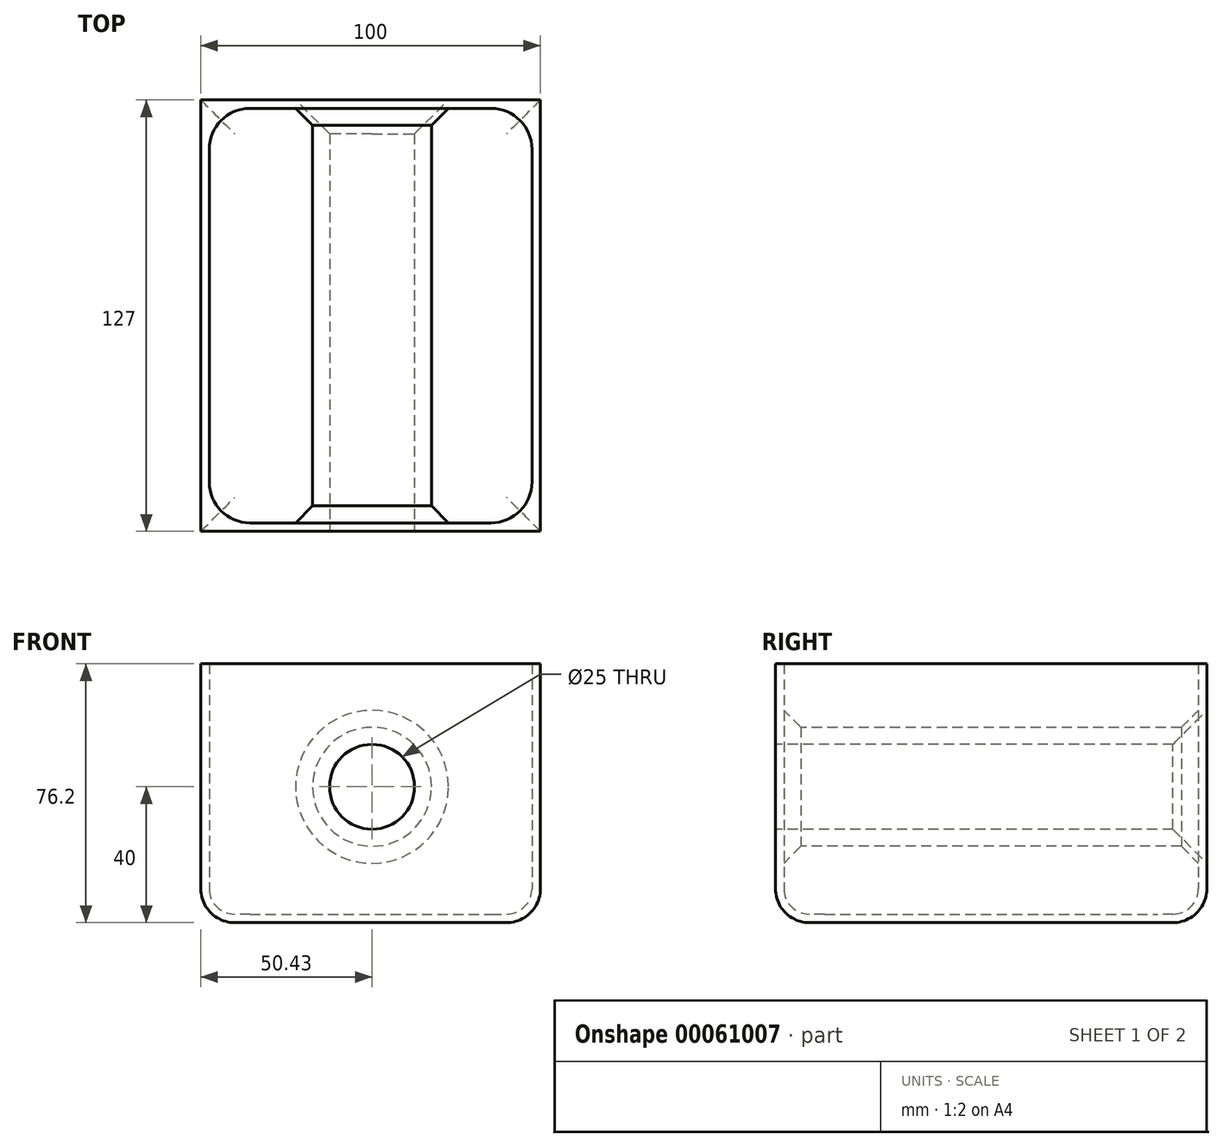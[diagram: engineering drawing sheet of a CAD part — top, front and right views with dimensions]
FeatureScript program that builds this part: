
annotation { "Feature Type Name" : "Feature", "Feature Type Description" : "" }
export const myFeature = defineFeature(function(context is Context, id is Id, definition is map)
    precondition{}
    {
        {
            var Q0;
            Q0=qCreatedBy(makeId("Top.planeOp"),FACE);
            var sketch = newSketch(context, id + "F0", { "sketchPlane" : qUnion([Q0])});
            skLineSegment(sketch, "E0.bottom", {"start": v(-50.43, -48.94) * mm, "end": v(49.57, -48.94) * mm});
            skLineSegment(sketch, "E0.top", {"start": v(-50.43, 78.06) * mm, "end": v(49.57, 78.06) * mm});
            skLineSegment(sketch, "E0.left", {"start": v(-50.43, -48.94) * mm, "end": v(-50.43, 78.06) * mm});
            skLineSegment(sketch, "E0.right", {"start": v(49.57, -48.94) * mm, "end": v(49.57, 78.06) * mm});
            skSolve(sketch);
        }
        {
            var Q0;
            Q0 = qSketchRegion(id + "F0", true);
            extrude(context, id + "F1", {"entities" : qUnion([Q0]), "depth" : 76.2 * mm});
        }
        {
            var Q0;
            Q0=makeQuery(id+"F1.opExtrude","CAP_FACE",FACE,{"disambiguationData":[OSD([sQuery(id+"F0.wireOp",EDGE,"E0.bottom"),sQuery(id+"F0.wireOp",EDGE,"E0.top"),sQuery(id+"F0.wireOp",EDGE,"E0.left"),sQuery(id+"F0.wireOp",EDGE,"E0.right")])],"isStart":true});
            fillet(context, id + "F2", {"entities" : qUnion([Q0]), "radius" : 10 * mm, "tangentPropagation" : true, "allowEdgeOverflow" : false});
        }
        {
            var Q0;
            Q0=makeQuery(id+"F1.opExtrude","CAP_FACE",FACE,{"disambiguationData":[OSD([sQuery(id+"F0.wireOp",EDGE,"E0.bottom"),sQuery(id+"F0.wireOp",EDGE,"E0.top"),sQuery(id+"F0.wireOp",EDGE,"E0.left"),sQuery(id+"F0.wireOp",EDGE,"E0.right")])],"isStart":false});
            shell(context, id + "F3", {"entities" : qUnion([Q0]), "thickness" : 2.5 * mm});
        }
        {
            var Q0;
            Q0=makeQuery(id+"F1.opExtrude","SWEPT_FACE",FACE,{"disambiguationData":[OSD([sQuery(id+"F0.wireOp",EDGE,"E0.bottom")])]});
            var sketch = newSketch(context, id + "F4", { "sketchPlane" : qUnion([Q0])});
            skCircle(sketch, "E1", {"center": v(0, 40) * mm, "radius": 17.5 * mm});
            skSolve(sketch);
        }
        {
            var Q0;
            Q0=makeQuery(id+"F4.imprint","IMPRINT",FACE,{"disambiguationData":[TD([[makeQuery(id+"F4.imprint","IMPRINT",EDGE,{"derivedFrom":sQuery(id+"F4.wireOp",EDGE,"E1")}),1.0]])]});
            var Q1;
            Q1=makeQuery(id+"F1.opExtrude","SWEPT_FACE",FACE,{"disambiguationData":[OSD([sQuery(id+"F0.wireOp",EDGE,"E0.top")])]});
            extrude(context, id + "F5", {"entities" : qUnion([Q0]), "operationType" : NewBodyOperationType.ADD, "endBound" : BoundingType.UP_TO_SURFACE, "oppositeDirection" : true, "endBoundEntityFace" : qUnion([Q1]), "depth" : 25 * mm});
        }
        {
            var Q0;
            Q0=makeQuery(id+"F1.opExtrude","SWEPT_FACE",FACE,{"disambiguationData":[OSD([sQuery(id+"F0.wireOp",EDGE,"E0.bottom")])]});
            var sketch = newSketch(context, id + "F6", { "sketchPlane" : qUnion([Q0])});
            skSolve(sketch);
        }
        {
            var Q0;
            {var subQ0=sQuery(id+"F0.wireOp",EDGE,"E0.bottom");Q0=makeQuery(id+"F6.imprint","IMPRINT",FACE,{"disambiguationData":[TD([[makeQuery(id+"F6.imprint","IMPRINT",EDGE,{"derivedFrom":makeQuery(id+"F1.opExtrude","CAP_EDGE",EDGE,{"disambiguationData":[OSD([subQ0])],"isStart":false})}),-1.0]])]});}
            var sketch = newSketch(context, id + "F7", { "sketchPlane" : qUnion([Q0])});
            skCircle(sketch, "E2.0", {"center": v(0, 40) * mm, "radius": 12.5 * mm});
            skSolve(sketch);
        }
        {
            var Q0;
            Q0=makeQuery(id+"F7.imprint","IMPRINT",FACE,{"disambiguationData":[TD([[makeQuery(id+"F7.imprint","IMPRINT",EDGE,{"derivedFrom":sQuery(id+"F7.wireOp",EDGE,"E2.0")}),1.0]])]});
            extrude(context, id + "F8", {"entities" : qUnion([Q0]), "operationType" : NewBodyOperationType.REMOVE, "endBound" : BoundingType.THROUGH_ALL, "oppositeDirection" : true, "depth" : 25 * mm});
        }
        {
            var Q0;
            {var subQ0=sQuery(id+"F0.wireOp",EDGE,"E0.top");Q0=makeQuery(id+"F5.boolean.opBoolean","INTERSECT",EDGE,{"derivedFrom":[makeQuery(id+"F3.opShell","OFFSET_FACE",FACE,{"disambiguationData":[OSD([subQ0]),TDD([makeQuery(id+"F1.opExtrude","SWEPT_FACE",FACE,{"disambiguationData":[OSD([subQ0])]})])]}),makeQuery(id+"F5.opExtrude","SWEPT_FACE",FACE,{"disambiguationData":[OSD([sQuery(id+"F4.wireOp",EDGE,"E1")])]})]});}
            var Q1;
            {var subQ0=sQuery(id+"F0.wireOp",EDGE,"E0.bottom");Q1=makeQuery(id+"F5.boolean.opBoolean","INTERSECT",EDGE,{"derivedFrom":[makeQuery(id+"F3.opShell","OFFSET_FACE",FACE,{"disambiguationData":[OSD([subQ0]),TDD([makeQuery(id+"F1.opExtrude","SWEPT_FACE",FACE,{"disambiguationData":[OSD([subQ0])]})])]}),makeQuery(id+"F5.opExtrude","SWEPT_FACE",FACE,{"disambiguationData":[OSD([sQuery(id+"F4.wireOp",EDGE,"E1")])]})]});}
            chamfer(context, id + "F9", {"entities" : qUnion([Q0, Q1]), "width" : 5 * mm, "tangentPropagation" : true});
        }
        {
            var Q0;
            Q0=makeQuery(id+"F8.boolean.opBoolean","COPY",EDGE,{"derivedFrom":makeQuery(id+"F8.opExtrude","CAP_EDGE",EDGE,{"disambiguationData":[OSD([sQuery(id+"F7.wireOp",EDGE,"E2.0")])],"isStart":true})});
            var Q1;
            Q1=makeQuery(id+"F8.boolean.opBoolean","INTERSECT",EDGE,{"derivedFrom":[makeQuery(id+"F1.opExtrude","SWEPT_FACE",FACE,{"disambiguationData":[OSD([sQuery(id+"F0.wireOp",EDGE,"E0.top")])]}),makeQuery(id+"F8.opExtrude","SWEPT_FACE",FACE,{"disambiguationData":[OSD([sQuery(id+"F7.wireOp",EDGE,"E2.0")])]})]});
            chamfer(context, id + "F10", {"entities" : qUnion([Q0, Q1]), "width" : 10 * mm, "tangentPropagation" : true});
        }
        {
            var Q0;
            {var subQ0=sQuery(id+"F0.wireOp",EDGE,"E0.left");var subQ1=sQuery(id+"F0.wireOp",EDGE,"E0.top");Q0=makeQuery(id+"F3.opShell","OFFSET_EDGE",EDGE,{"disambiguationData":[OSD([subQ1,subQ0]),TDD([makeQuery(id+"F1.opExtrude","SWEPT_EDGE",EDGE,{"disambiguationData":[OSD([subQ1,subQ0])]})])]});}
            var Q1;
            {var subQ0=sQuery(id+"F0.wireOp",EDGE,"E0.right");var subQ1=sQuery(id+"F0.wireOp",EDGE,"E0.top");Q1=makeQuery(id+"F3.opShell","OFFSET_EDGE",EDGE,{"disambiguationData":[OSD([subQ1,subQ0]),TDD([makeQuery(id+"F1.opExtrude","SWEPT_EDGE",EDGE,{"disambiguationData":[OSD([subQ1,subQ0])]})])]});}
            var Q2;
            {var subQ0=sQuery(id+"F0.wireOp",EDGE,"E0.right");var subQ1=sQuery(id+"F0.wireOp",EDGE,"E0.bottom");Q2=makeQuery(id+"F3.opShell","OFFSET_EDGE",EDGE,{"disambiguationData":[OSD([subQ1,subQ0]),TDD([makeQuery(id+"F1.opExtrude","SWEPT_EDGE",EDGE,{"disambiguationData":[OSD([subQ1,subQ0])]})])]});}
            var Q3;
            {var subQ0=sQuery(id+"F0.wireOp",EDGE,"E0.left");var subQ1=sQuery(id+"F0.wireOp",EDGE,"E0.bottom");Q3=makeQuery(id+"F3.opShell","OFFSET_EDGE",EDGE,{"disambiguationData":[OSD([subQ1,subQ0]),TDD([makeQuery(id+"F1.opExtrude","SWEPT_EDGE",EDGE,{"disambiguationData":[OSD([subQ1,subQ0])]})])]});}
            fillet(context, id + "F11", {"entities" : qUnion([Q0, Q1, Q2, Q3]), "radius" : 12 * mm, "tangentPropagation" : true, "allowEdgeOverflow" : false});
        }
    });
